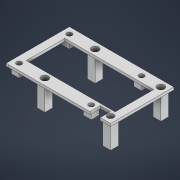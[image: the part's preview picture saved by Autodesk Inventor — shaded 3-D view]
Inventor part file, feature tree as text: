
AUTODESK INVENTOR PART (.ipt)
format: ipt  version: 2021 (Build 250183000, 183)  size: 317,952 bytes
history: native  units: mm
features: extrude x12, sketch x11
ambient origin geometry x8: Origin, YZ Plane, XZ Plane, XY Plane, X Axis, Y Axis, Z Axis, Center Point
bodies: Volumenkörper1 (feature_tree)
feature tree (23):
  sketch  "Skizze1"  dims[d0=57.0mm d1=45.0mm]
  extrude  "Extrusion1"  Depth=45.0mm
  extrude  "Extrusion2"  Depth=3.2mm
  extrude  "Extrusion3"  Depth=3.2mm
  extrude  "Extrusion4"  Depth=39.0mm
  extrude  "Extrusion5"  Depth=51.0mm
  extrude  "Extrusion6"  Depth=39.0mm
  extrude  "Extrusion7"  Depth=3.0mm
  extrude  "Extrusion8"  Depth=6.0mm
  extrude  "Extrusion9"  Depth=8.0mm
  sketch  "Skizze7"  dims[d13=3.0mm d14=25.5mm]
  extrude  "Extrusion10"  Depth=6.0mm
  extrude  "Extrusion11"  Depth=6.0mm
  extrude  "Extrusion12"  Depth=6.0mm
  sketch  "Skizze2"  dims[d2=3.2mm d3=3.2mm]
  sketch  "Skizze3"  dims[d4=3.2mm d5=3.2mm]
  sketch  "Skizze4"  dims[d6=39.0mm d7=19.5mm]
  sketch  "Skizze5"  dims[d8=51.0mm d9=51.0mm]
  sketch  "Skizze6"  dims[d10=39.0mm d11=19.5mm]
  sketch  "Skizze8"  dims[d15=6.0mm d16=6.0mm]
  sketch  "Skizze9"  dims[d17=0.0mm d18=8.0mm]
  sketch  "Skizze10"  dims[d19=6.0mm d20=6.0mm]
  sketch  "Skizze11"  dims[d21=6.0mm d22=6.0mm d23=6.0mm d24=6.0mm d25=2.0mm d26=0.0mm d27=23.0mm d28=0.0mm d29=2.0mm d30=0.0mm d31=20.0mm d32=0.0mm d33=4.0mm d34=4.0mm d35=39.0mm d36=19.5mm d37=18.0mm d38=18.0mm d39=4.0mm d40=4.0mm d41=3.0mm d42=3.0mm d43=56.0mm d44=56.0mm d45=6.0mm d46=6.0mm d47=6.0mm d48=6.0mm d49=6.0mm d50=6.0mm d51=15.0mm d52=6.0mm d53=6.0mm d54=15.0mm d55=5.0mm d56=0.0mm d57=6.0mm d58=0.0mm d59=3.2mm d60=3.2mm d61=3.2mm d62=3.2mm d63=3.0mm d64=3.0mm d65=5.0mm d66=0.0mm d67=69.0mm d68=30.0mm d69=4.0mm d70=0.0mm d71=0.0mm d72=5.5mm d73=63.0mm d74=6.0mm d75=0.0mm d76=2.0mm d77=0.0mm d78=2.0mm d79=0.0mm d80=5.0mm d81=5.5mm d82=5.5mm d83=2.0mm d84=0.0mm d85=2.0mm d86=0.0mm d87=4.0mm d88=0.0mm]
